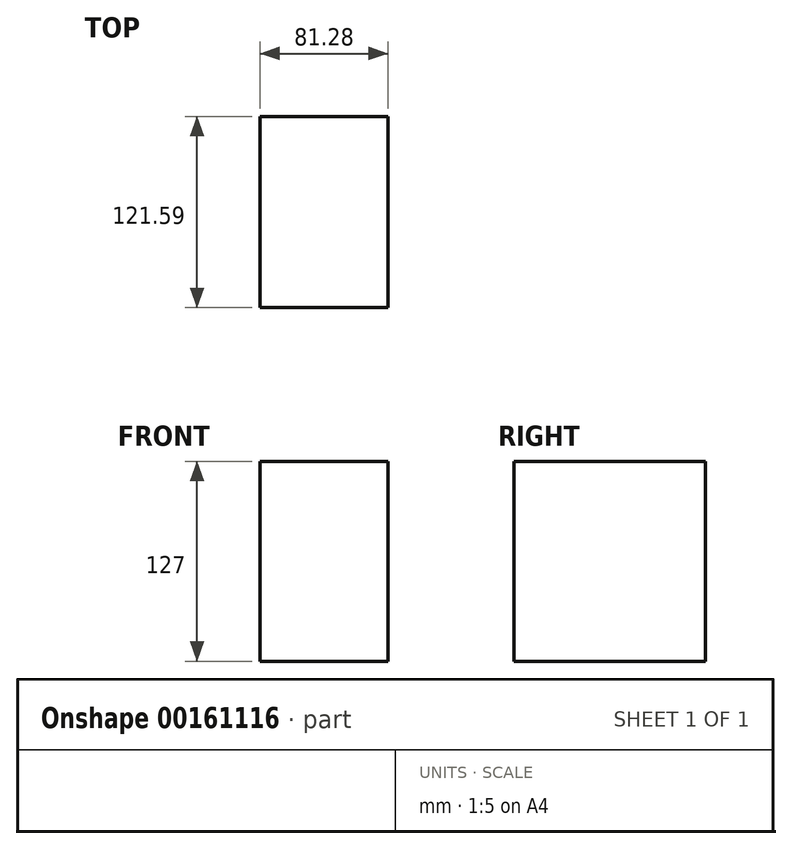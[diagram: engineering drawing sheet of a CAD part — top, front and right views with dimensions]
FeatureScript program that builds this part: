
annotation { "Feature Type Name" : "Feature", "Feature Type Description" : "" }
export const myFeature = defineFeature(function(context is Context, id is Id, definition is map)
    precondition{}
    {
        {
            var Q0;
            Q0=qCreatedBy(makeId("Front.planeOp"),FACE);
            var sketch = newSketch(context, id + "F0", { "sketchPlane" : qUnion([Q0])});
            skLineSegment(sketch, "E0.bottom", {"start": v(-81.28, -15.4) * mm, "end": v(0, -15.4) * mm});
            skLineSegment(sketch, "E0.top", {"start": v(-81.28, 111.6) * mm, "end": v(0, 111.6) * mm});
            skLineSegment(sketch, "E0.left", {"start": v(-81.28, -15.4) * mm, "end": v(-81.28, 111.6) * mm});
            skLineSegment(sketch, "E0.right", {"start": v(0, -15.4) * mm, "end": v(0, 111.6) * mm});
            skSolve(sketch);
        }
        {
            var Q0;
            Q0=makeQuery(id+"F0.imprint","IMPRINT",FACE,{"disambiguationData":[TD([[makeQuery(id+"F0.imprint","IMPRINT",EDGE,{"derivedFrom":sQuery(id+"F0.wireOp",EDGE,"E0.bottom")}),1.0]])]});
            extrude(context, id + "F1", {"entities" : qUnion([Q0]), "depth" : 121.6 * mm});
        }
    });
